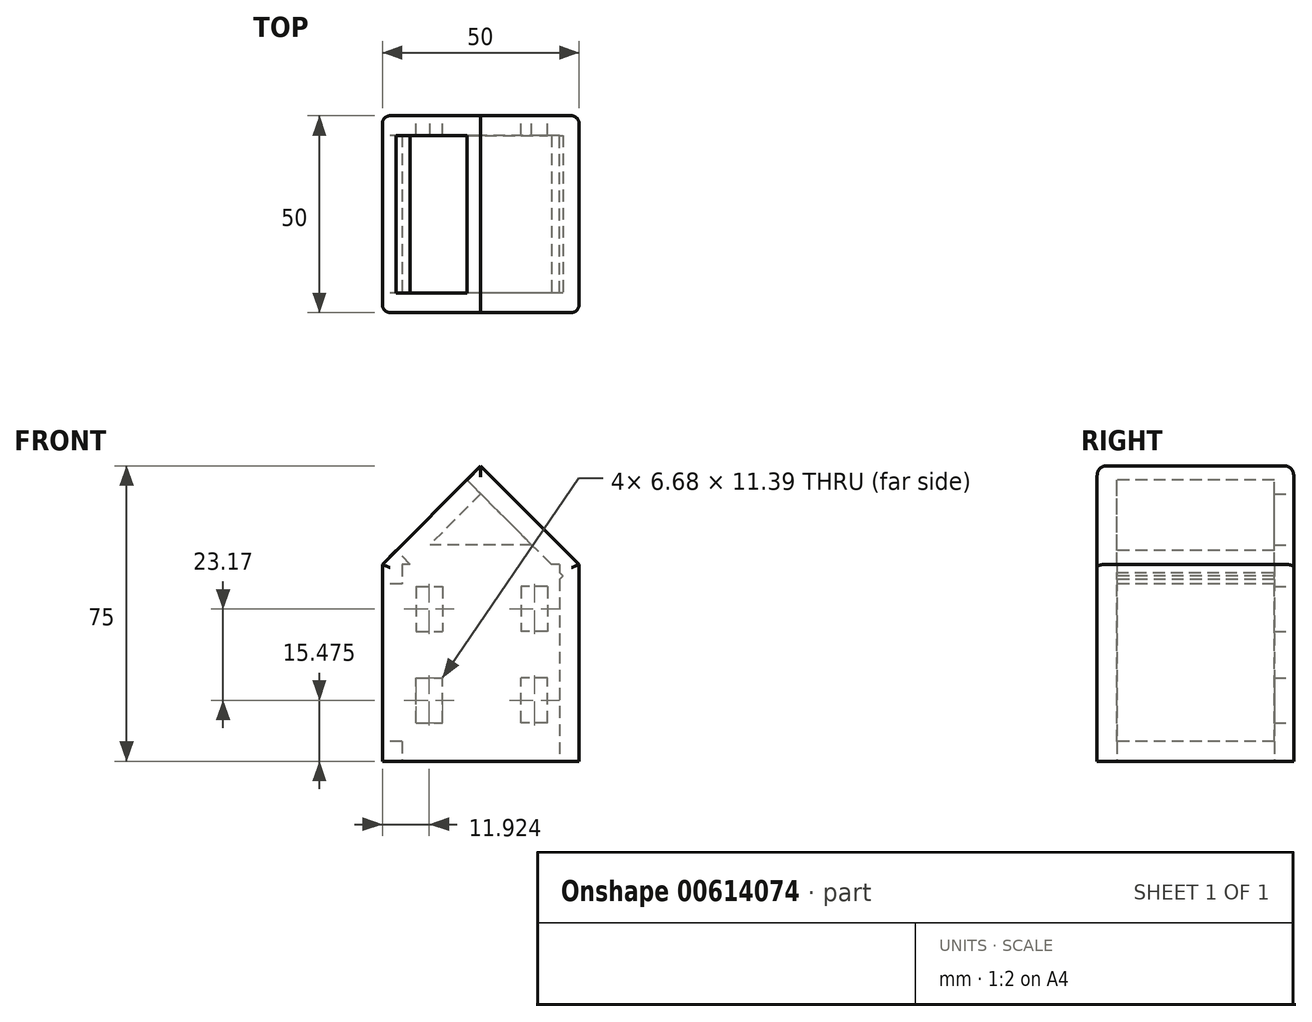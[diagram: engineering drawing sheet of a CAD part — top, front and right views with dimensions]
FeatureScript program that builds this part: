
annotation { "Feature Type Name" : "Feature", "Feature Type Description" : "" }
export const myFeature = defineFeature(function(context is Context, id is Id, definition is map)
    precondition{}
    {
        {
            var Q0;
            Q0=qCreatedBy(makeId("Top.planeOp"),FACE);
            var sketch = newSketch(context, id + "F0", { "sketchPlane" : qUnion([Q0])});
            skLineSegment(sketch, "E0.bottom", {"start": v(0, 0) * mm, "end": v(50, 0) * mm});
            skLineSegment(sketch, "E0.top", {"start": v(0, 50) * mm, "end": v(50, 50) * mm});
            skLineSegment(sketch, "E0.left", {"start": v(0, 0) * mm, "end": v(0, 50) * mm});
            skLineSegment(sketch, "E0.right", {"start": v(50, 0) * mm, "end": v(50, 50) * mm});
            skSolve(sketch);
        }
        {
            var Q0;
            Q0 = qSketchRegion(id + "F0", true);
            extrude(context, id + "F1", {"entities" : qUnion([Q0]), "depth" : 50 * mm, "offsetDistance" : 25 * mm});
        }
        {
            var Q0;
            Q0=makeQuery(id+"F1.opExtrude","CAP_FACE",FACE,{"disambiguationData":[OSD([sQuery(id+"F0.wireOp",EDGE,"E0.bottom"),sQuery(id+"F0.wireOp",EDGE,"E0.top"),sQuery(id+"F0.wireOp",EDGE,"E0.left"),sQuery(id+"F0.wireOp",EDGE,"E0.right")])],"isStart":false});
            var sketch = newSketch(context, id + "F2", { "sketchPlane" : qUnion([Q0])});
            skLineSegment(sketch, "E1.bottom", {"start": v(0, 50) * mm, "end": v(50, 50) * mm});
            skLineSegment(sketch, "E1.top", {"start": v(0, 0) * mm, "end": v(50, 0) * mm});
            skLineSegment(sketch, "E1.left", {"start": v(0, 50) * mm, "end": v(0, 0) * mm});
            skLineSegment(sketch, "E1.right", {"start": v(50, 50) * mm, "end": v(50, 0) * mm});
            skSolve(sketch);
        }
        {
            var Q0;
            Q0=makeQuery(id+"F1.opExtrude","CAP_FACE",FACE,{"disambiguationData":[OSD([sQuery(id+"F0.wireOp",EDGE,"E0.bottom"),sQuery(id+"F0.wireOp",EDGE,"E0.top"),sQuery(id+"F0.wireOp",EDGE,"E0.left"),sQuery(id+"F0.wireOp",EDGE,"E0.right")])],"isStart":false});
            extrude(context, id + "F3", {"entities" : qUnion([Q0]), "operationType" : NewBodyOperationType.ADD, "depth" : 25 * mm, "offsetDistance" : 25 * mm});
        }
        {
            var Q0;
            Q0=makeQuery(id+"F3.opExtrude","CAP_EDGE",EDGE,{"disambiguationData":[OSD([sQuery(id+"F0.wireOp",EDGE,"E0.right")])],"isStart":false});
            var Q1;
            Q1=makeQuery(id+"F3.opExtrude","CAP_EDGE",EDGE,{"disambiguationData":[OSD([sQuery(id+"F0.wireOp",EDGE,"E0.left")])],"isStart":false});
            chamfer(context, id + "F4", {"entities" : qUnion([Q0, Q1]), "width" : 25 * mm, "tangentPropagation" : true});
        }
        {
            var Q0;
            Q0=makeQuery(id+"F0.imprint","IMPRINT",FACE,{"disambiguationData":[TD([[makeQuery(id+"F0.imprint","IMPRINT",EDGE,{"derivedFrom":sQuery(id+"F0.wireOp",EDGE,"E0.bottom")}),1.0]])]});
            var sketch = newSketch(context, id + "F5", { "sketchPlane" : qUnion([Q0])});
            skLineSegment(sketch, "E2.bottom", {"start": v(45, 45) * mm, "end": v(5, 45) * mm});
            skLineSegment(sketch, "E2.top", {"start": v(45, 5) * mm, "end": v(5, 5) * mm});
            skLineSegment(sketch, "E2.left", {"start": v(45, 45) * mm, "end": v(45, 5) * mm});
            skLineSegment(sketch, "E2.right", {"start": v(5, 45) * mm, "end": v(5, 5) * mm});
            skPoint(sketch, "E2.middle", {"position": v(25, 25) * mm});
            skPoint(sketch, "E3.endSnap0", {"position": v(5, 25) * mm});
            skPoint(sketch, "E4.endSnap0", {"position": v(25, 5) * mm});
            skSolve(sketch);
        }
        {
            var Q0;
            Q0=makeQuery(id+"F5.imprint","IMPRINT",FACE,{"disambiguationData":[TD([[makeQuery(id+"F5.imprint","IMPRINT",EDGE,{"derivedFrom":sQuery(id+"F5.wireOp",EDGE,"E2.bottom")}),1.0]])]});
            var Q1;
            Q1=makeQuery(id+"F1.opExtrude","CAP_FACE",FACE,{"disambiguationData":[OSD([sQuery(id+"F0.wireOp",EDGE,"E0.bottom"),sQuery(id+"F0.wireOp",EDGE,"E0.top"),sQuery(id+"F0.wireOp",EDGE,"E0.left"),sQuery(id+"F0.wireOp",EDGE,"E0.right")])],"isStart":true});
            extrude(context, id + "F6", {"entities" : qUnion([Q0]), "operationType" : NewBodyOperationType.REMOVE, "depth" : 50 * mm, "endBoundEntityFace" : qUnion([Q1]), "hasOffset" : true, "offsetDistance" : 25 * mm, "offsetOppositeDirection" : true});
        }
        {
            var Q0;
            {var subQ0=sQuery(id+"F0.wireOp",EDGE,"E0.left");Q0=makeQuery(id+"F3.boolean.opBoolean","MERGE",FACE,{"derivedFrom":[makeQuery(id+"F1.opExtrude","SWEPT_FACE",FACE,{"disambiguationData":[OSD([subQ0])]}),makeQuery(id+"F3.opExtrude","SWEPT_FACE",FACE,{"disambiguationData":[OSD([subQ0])]})]});}
            var sketch = newSketch(context, id + "F7", { "sketchPlane" : qUnion([Q0])});
            skLineSegment(sketch, "E5.bottom", {"start": v(-45, 5) * mm, "end": v(-5, 5) * mm});
            skLineSegment(sketch, "E5.top", {"start": v(-45, 45) * mm, "end": v(-5, 45) * mm});
            skLineSegment(sketch, "E5.left", {"start": v(-45, 5) * mm, "end": v(-45, 45) * mm});
            skLineSegment(sketch, "E5.right", {"start": v(-5, 5) * mm, "end": v(-5, 45) * mm});
            skPoint(sketch, "E5.middle", {"position": v(-25, 25) * mm});
            skSolve(sketch);
        }
        {
            var Q0;
            Q0 = qSketchRegion(id + "F7", true);
            extrude(context, id + "F8", {"entities" : qUnion([Q0]), "operationType" : NewBodyOperationType.REMOVE, "oppositeDirection" : true, "depth" : 5 * mm, "offsetDistance" : 25 * mm});
        }
        {
            var Q0;
            Q0=makeQuery(id+"F4.opChamfer","BLEND_FACE",FACE,{"disambiguationData":[OSD([sQuery(id+"F0.wireOp",EDGE,"E0.left")])]});
            var sketch = newSketch(context, id + "F9", { "sketchPlane" : qUnion([Q0])});
            skLineSegment(sketch, "E6.bottom", {"start": v(-45, 40.36) * mm, "end": v(-5, 40.36) * mm});
            skLineSegment(sketch, "E6.top", {"start": v(-45, 65.71) * mm, "end": v(-5, 65.71) * mm});
            skLineSegment(sketch, "E6.left", {"start": v(-45, 40.36) * mm, "end": v(-45, 65.71) * mm});
            skLineSegment(sketch, "E6.right", {"start": v(-5, 40.36) * mm, "end": v(-5, 65.71) * mm});
            skPoint(sketch, "E6.middle", {"position": v(-25, 53.03) * mm});
            skSolve(sketch);
        }
        {
            var Q0;
            Q0 = qSketchRegion(id + "F9", true);
            extrude(context, id + "F10", {"entities" : qUnion([Q0]), "operationType" : NewBodyOperationType.REMOVE, "oppositeDirection" : true, "depth" : 34.5 * mm, "offsetDistance" : 25 * mm});
        }
        {
            var Q0;
            {var subQ0=sQuery(id+"F0.wireOp",EDGE,"E0.top");Q0=makeQuery(id+"F3.boolean.opBoolean","MERGE",FACE,{"derivedFrom":[makeQuery(id+"F1.opExtrude","SWEPT_FACE",FACE,{"disambiguationData":[OSD([subQ0])]}),makeQuery(id+"F3.opExtrude","SWEPT_FACE",FACE,{"disambiguationData":[OSD([subQ0])]})]});}
            var sketch = newSketch(context, id + "F11", { "sketchPlane" : qUnion([Q0])});
            skLineSegment(sketch, "E7", {"start": v(-37.93, 55) * mm, "end": v(-25, 67.93) * mm});
            skLineSegment(sketch, "E8", {"start": v(-25, 67.93) * mm, "end": v(-12.07, 55) * mm});
            skLineSegment(sketch, "E9", {"start": v(-12.07, 55) * mm, "end": v(-25, 55) * mm});
            skLineSegment(sketch, "E10", {"start": v(-37.93, 55) * mm, "end": v(-25, 55) * mm});
            skSolve(sketch);
        }
        {
            var Q0;
            Q0=makeQuery(id+"F11.imprint","IMPRINT",FACE,{"disambiguationData":[TD([[makeQuery(id+"F11.imprint","IMPRINT",EDGE,{"derivedFrom":sQuery(id+"F11.wireOp",EDGE,"E7")}),1.0]])]});
            var sketch = newSketch(context, id + "F12", { "sketchPlane" : qUnion([Q0])});
            skLineSegment(sketch, "E11.bottom", {"start": v(-41.97, 44.34) * mm, "end": v(-35.29, 44.34) * mm});
            skLineSegment(sketch, "E11.top", {"start": v(-41.97, 32.95) * mm, "end": v(-35.29, 32.95) * mm});
            skLineSegment(sketch, "E11.left", {"start": v(-41.97, 44.34) * mm, "end": v(-41.97, 32.95) * mm});
            skLineSegment(sketch, "E11.right", {"start": v(-35.29, 44.34) * mm, "end": v(-35.29, 32.95) * mm});
            skPoint(sketch, "E11.middle", {"position": v(-38.63, 38.64) * mm});
            skLineSegment(sketch, "E12.MirrorCS", {"start": v(-8.59, 32.95) * mm, "end": v(-15.26, 32.95) * mm});
            skLineSegment(sketch, "E13.MirrorCS", {"start": v(-8.59, 44.34) * mm, "end": v(-8.59, 32.95) * mm});
            skLineSegment(sketch, "E14.MirrorCS", {"start": v(-8.59, 44.34) * mm, "end": v(-15.26, 44.34) * mm});
            skLineSegment(sketch, "E15.MirrorCS", {"start": v(-15.26, 44.34) * mm, "end": v(-15.26, 32.95) * mm});
            skLineSegment(sketch, "E16.MirrorCS", {"start": v(-41.97, 9.78) * mm, "end": v(-41.97, 21.17) * mm});
            skLineSegment(sketch, "E17.MirrorCS", {"start": v(-41.97, 9.78) * mm, "end": v(-35.29, 9.78) * mm});
            skLineSegment(sketch, "E18.MirrorCS", {"start": v(-35.29, 9.78) * mm, "end": v(-35.29, 21.17) * mm});
            skLineSegment(sketch, "E19.MirrorCS", {"start": v(-8.59, 21.17) * mm, "end": v(-15.26, 21.17) * mm});
            skLineSegment(sketch, "E20.MirrorCS", {"start": v(-15.26, 9.78) * mm, "end": v(-15.26, 21.17) * mm});
            skLineSegment(sketch, "E21.MirrorCS", {"start": v(-8.59, 9.78) * mm, "end": v(-15.26, 9.78) * mm});
            skLineSegment(sketch, "E22.MirrorCS", {"start": v(-8.59, 9.78) * mm, "end": v(-8.59, 21.17) * mm});
            skLineSegment(sketch, "E23.MirrorCS", {"start": v(-41.97, 21.17) * mm, "end": v(-35.29, 21.17) * mm});
            skSolve(sketch);
        }
        {
            var Q0;
            Q0 = qSketchRegion(id + "F12", true);
            extrude(context, id + "F13", {"entities" : qUnion([Q0]), "operationType" : NewBodyOperationType.REMOVE, "oppositeDirection" : true, "depth" : 10 * mm, "offsetDistance" : 25 * mm});
        }
        {
            var Q0;
            Q0=makeQuery(id+"F11.imprint","IMPRINT",FACE,{"disambiguationData":[TD([[makeQuery(id+"F11.imprint","IMPRINT",EDGE,{"derivedFrom":sQuery(id+"F11.wireOp",EDGE,"E7")}),-1.0]])]});
            extrude(context, id + "F14", {"entities" : qUnion([Q0]), "operationType" : NewBodyOperationType.REMOVE, "oppositeDirection" : true, "depth" : 10 * mm, "offsetDistance" : 25 * mm});
        }
        {
            var Q0;
            {var subQ0=sQuery(id+"F0.wireOp",EDGE,"E0.left");var subQ1=sQuery(id+"F0.wireOp",EDGE,"E0.top");Q0=makeQuery(id+"F3.boolean.opBoolean","MERGE",EDGE,{"derivedFrom":[makeQuery(id+"F1.opExtrude","SWEPT_EDGE",EDGE,{"disambiguationData":[OSD([subQ1,subQ0])]}),makeQuery(id+"F3.opExtrude","SWEPT_EDGE",EDGE,{"disambiguationData":[OSD([subQ1,subQ0])]})]});}
            var Q1;
            {var subQ0=sQuery(id+"F0.wireOp",EDGE,"E0.right");var subQ1=sQuery(id+"F0.wireOp",EDGE,"E0.top");Q1=makeQuery(id+"F3.boolean.opBoolean","MERGE",EDGE,{"derivedFrom":[makeQuery(id+"F1.opExtrude","SWEPT_EDGE",EDGE,{"disambiguationData":[OSD([subQ1,subQ0])]}),makeQuery(id+"F3.opExtrude","SWEPT_EDGE",EDGE,{"disambiguationData":[OSD([subQ1,subQ0])]})]});}
            var Q2;
            {var subQ0=sQuery(id+"F0.wireOp",EDGE,"E0.top");Q2=makeQuery(id+"F4.opChamfer","BLEND_EDGE",EDGE,{"blendedFrom":[makeQuery(id+"F3.opExtrude","CAP_EDGE",EDGE,{"disambiguationData":[OSD([sQuery(id+"F0.wireOp",EDGE,"E0.right")])],"isStart":false}),makeQuery(id+"F3.boolean.opBoolean","MERGE",FACE,{"derivedFrom":[makeQuery(id+"F1.opExtrude","SWEPT_FACE",FACE,{"disambiguationData":[OSD([subQ0])]}),makeQuery(id+"F3.opExtrude","SWEPT_FACE",FACE,{"disambiguationData":[OSD([subQ0])]})]})],"blendedInto":[makeQuery(id+"F3.boolean.opBoolean","MERGE",FACE,{"derivedFrom":[makeQuery(id+"F1.opExtrude","SWEPT_FACE",FACE,{"disambiguationData":[OSD([subQ0])]}),makeQuery(id+"F3.opExtrude","SWEPT_FACE",FACE,{"disambiguationData":[OSD([subQ0])]})]})]});}
            var Q3;
            {var subQ0=sQuery(id+"F0.wireOp",EDGE,"E0.top");Q3=makeQuery(id+"F4.opChamfer","BLEND_EDGE",EDGE,{"blendedFrom":[makeQuery(id+"F3.opExtrude","CAP_EDGE",EDGE,{"disambiguationData":[OSD([sQuery(id+"F0.wireOp",EDGE,"E0.left")])],"isStart":false}),makeQuery(id+"F3.boolean.opBoolean","MERGE",FACE,{"derivedFrom":[makeQuery(id+"F1.opExtrude","SWEPT_FACE",FACE,{"disambiguationData":[OSD([subQ0])]}),makeQuery(id+"F3.opExtrude","SWEPT_FACE",FACE,{"disambiguationData":[OSD([subQ0])]})]})],"blendedInto":[makeQuery(id+"F3.boolean.opBoolean","MERGE",FACE,{"derivedFrom":[makeQuery(id+"F1.opExtrude","SWEPT_FACE",FACE,{"disambiguationData":[OSD([subQ0])]}),makeQuery(id+"F3.opExtrude","SWEPT_FACE",FACE,{"disambiguationData":[OSD([subQ0])]})]})]});}
            var Q4;
            {var subQ0=sQuery(id+"F0.wireOp",EDGE,"E0.bottom");Q4=makeQuery(id+"F4.opChamfer","BLEND_EDGE",EDGE,{"blendedFrom":[makeQuery(id+"F3.opExtrude","CAP_EDGE",EDGE,{"disambiguationData":[OSD([sQuery(id+"F0.wireOp",EDGE,"E0.left")])],"isStart":false}),makeQuery(id+"F3.boolean.opBoolean","MERGE",FACE,{"derivedFrom":[makeQuery(id+"F1.opExtrude","SWEPT_FACE",FACE,{"disambiguationData":[OSD([subQ0])]}),makeQuery(id+"F3.opExtrude","SWEPT_FACE",FACE,{"disambiguationData":[OSD([subQ0])]})]})],"blendedInto":[makeQuery(id+"F3.boolean.opBoolean","MERGE",FACE,{"derivedFrom":[makeQuery(id+"F1.opExtrude","SWEPT_FACE",FACE,{"disambiguationData":[OSD([subQ0])]}),makeQuery(id+"F3.opExtrude","SWEPT_FACE",FACE,{"disambiguationData":[OSD([subQ0])]})]})]});}
            var Q5;
            {var subQ0=sQuery(id+"F0.wireOp",EDGE,"E0.left");var subQ1=sQuery(id+"F0.wireOp",EDGE,"E0.bottom");Q5=makeQuery(id+"F3.boolean.opBoolean","MERGE",EDGE,{"derivedFrom":[makeQuery(id+"F1.opExtrude","SWEPT_EDGE",EDGE,{"disambiguationData":[OSD([subQ1,subQ0])]}),makeQuery(id+"F3.opExtrude","SWEPT_EDGE",EDGE,{"disambiguationData":[OSD([subQ1,subQ0])]})]});}
            var Q6;
            {var subQ0=sQuery(id+"F0.wireOp",EDGE,"E0.bottom");Q6=makeQuery(id+"F4.opChamfer","BLEND_EDGE",EDGE,{"blendedFrom":[makeQuery(id+"F3.opExtrude","CAP_EDGE",EDGE,{"disambiguationData":[OSD([sQuery(id+"F0.wireOp",EDGE,"E0.right")])],"isStart":false}),makeQuery(id+"F3.boolean.opBoolean","MERGE",FACE,{"derivedFrom":[makeQuery(id+"F1.opExtrude","SWEPT_FACE",FACE,{"disambiguationData":[OSD([subQ0])]}),makeQuery(id+"F3.opExtrude","SWEPT_FACE",FACE,{"disambiguationData":[OSD([subQ0])]})]})],"blendedInto":[makeQuery(id+"F3.boolean.opBoolean","MERGE",FACE,{"derivedFrom":[makeQuery(id+"F1.opExtrude","SWEPT_FACE",FACE,{"disambiguationData":[OSD([subQ0])]}),makeQuery(id+"F3.opExtrude","SWEPT_FACE",FACE,{"disambiguationData":[OSD([subQ0])]})]})]});}
            var Q7;
            {var subQ0=sQuery(id+"F0.wireOp",EDGE,"E0.right");var subQ1=sQuery(id+"F0.wireOp",EDGE,"E0.bottom");Q7=makeQuery(id+"F3.boolean.opBoolean","MERGE",EDGE,{"derivedFrom":[makeQuery(id+"F1.opExtrude","SWEPT_EDGE",EDGE,{"disambiguationData":[OSD([subQ1,subQ0])]}),makeQuery(id+"F3.opExtrude","SWEPT_EDGE",EDGE,{"disambiguationData":[OSD([subQ1,subQ0])]})]});}
            var Q8;
            Q8=makeQuery(id+"F14.boolean.opBoolean","COPY",EDGE,{"derivedFrom":makeQuery(id+"F14.opExtrude","CAP_EDGE",EDGE,{"disambiguationData":[OSD([sQuery(id+"F11.wireOp",EDGE,"E9"),sQuery(id+"F11.wireOp",EDGE,"E10")])],"isStart":true})});
            var Q9;
            Q9=makeQuery(id+"F14.boolean.opBoolean","COPY",EDGE,{"derivedFrom":makeQuery(id+"F14.opExtrude","CAP_EDGE",EDGE,{"disambiguationData":[OSD([sQuery(id+"F11.wireOp",EDGE,"E8")])],"isStart":true})});
            var Q10;
            Q10=makeQuery(id+"F14.boolean.opBoolean","COPY",EDGE,{"derivedFrom":makeQuery(id+"F14.opExtrude","CAP_EDGE",EDGE,{"disambiguationData":[OSD([sQuery(id+"F11.wireOp",EDGE,"E7")])],"isStart":true})});
            var Q11;
            Q11=makeQuery(id+"F13.boolean.opBoolean","COPY",EDGE,{"derivedFrom":makeQuery(id+"F13.opExtrude","CAP_EDGE",EDGE,{"disambiguationData":[OSD([sQuery(id+"F12.wireOp",EDGE,"E11.top")])],"isStart":true})});
            var Q12;
            Q12=makeQuery(id+"F13.boolean.opBoolean","COPY",EDGE,{"derivedFrom":makeQuery(id+"F13.opExtrude","CAP_EDGE",EDGE,{"disambiguationData":[OSD([sQuery(id+"F12.wireOp",EDGE,"E12.MirrorCS")])],"isStart":true})});
            var Q13;
            Q13=makeQuery(id+"F13.boolean.opBoolean","COPY",EDGE,{"derivedFrom":makeQuery(id+"F13.opExtrude","CAP_EDGE",EDGE,{"disambiguationData":[OSD([sQuery(id+"F12.wireOp",EDGE,"E17.MirrorCS")])],"isStart":true})});
            var Q14;
            Q14=makeQuery(id+"F13.boolean.opBoolean","COPY",EDGE,{"derivedFrom":makeQuery(id+"F13.opExtrude","CAP_EDGE",EDGE,{"disambiguationData":[OSD([sQuery(id+"F12.wireOp",EDGE,"E21.MirrorCS")])],"isStart":true})});
            var Q15;
            Q15=makeQuery(id+"F10.boolean.opBoolean","COPY",EDGE,{"derivedFrom":makeQuery(id+"F10.opExtrude","CAP_EDGE",EDGE,{"disambiguationData":[OSD([sQuery(id+"F9.wireOp",EDGE,"E6.left")])],"isStart":true})});
            var Q16;
            Q16=makeQuery(id+"F10.boolean.opBoolean","COPY",EDGE,{"derivedFrom":makeQuery(id+"F10.opExtrude","CAP_EDGE",EDGE,{"disambiguationData":[OSD([sQuery(id+"F9.wireOp",EDGE,"E6.top")])],"isStart":true})});
            var Q17;
            Q17=makeQuery(id+"F10.boolean.opBoolean","COPY",EDGE,{"derivedFrom":makeQuery(id+"F10.opExtrude","CAP_EDGE",EDGE,{"disambiguationData":[OSD([sQuery(id+"F9.wireOp",EDGE,"E6.right")])],"isStart":true})});
            var Q18;
            Q18=makeQuery(id+"F10.boolean.opBoolean","COPY",EDGE,{"derivedFrom":makeQuery(id+"F10.opExtrude","CAP_EDGE",EDGE,{"disambiguationData":[OSD([sQuery(id+"F9.wireOp",EDGE,"E6.bottom")])],"isStart":true})});
            fillet(context, id + "F15", {"entities" : qUnion([Q0, Q1, Q2, Q3, Q4, Q5, Q6, Q7, Q8, Q9, Q10, Q11, Q12, Q13, Q14, Q15, Q16, Q17, Q18]), "radius" : 2 * mm, "tangentPropagation" : true, "allowEdgeOverflow" : false});
        }
    });
